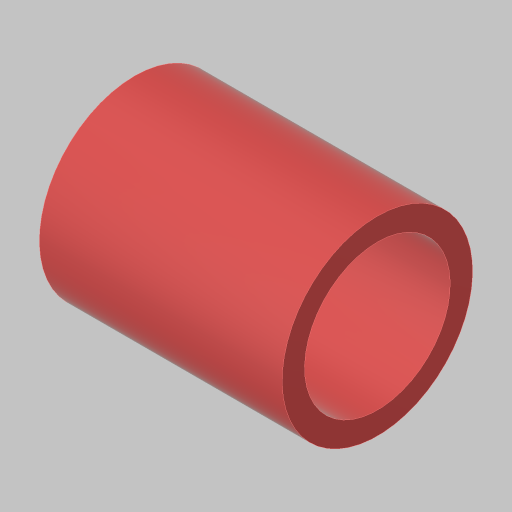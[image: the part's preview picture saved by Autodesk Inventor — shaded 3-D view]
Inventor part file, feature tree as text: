
AUTODESK INVENTOR PART (.ipt)
format: ipt  version: 2023.5 (Build 275446000, 446)  size: 117,248 bytes
history: native  units: in
note: dims shown in document units (in); Inventor stores cm internally (conversion verified against a paired STEP export)
features: extrude x1, sketch x1
ambient origin geometry x8: Origin, YZ Plane, XZ Plane, XY Plane, X Axis, Y Axis, Z Axis, Center Point
bodies: Solid1 (feature_tree)
feature tree (2):
  extrude  "Extrusion1"  Depth=0.975in
  sketch  "Sketch1"  dims[d0=0.585in d1=0.09in d2=0.975in d3=0.0in]
